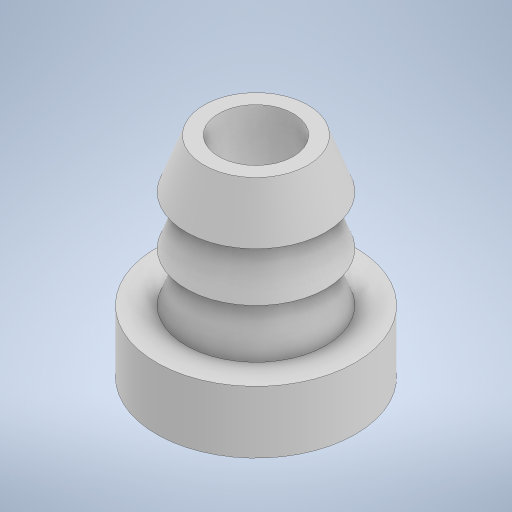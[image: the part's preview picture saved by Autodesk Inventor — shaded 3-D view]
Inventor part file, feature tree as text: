
AUTODESK INVENTOR PART (.ipt)
format: ipt  version: 2024.2 (Build 282272000, 272)  size: 631,808 bytes
history: native  units: in
note: dims shown in document units (in); Inventor stores cm internally (conversion verified against a paired STEP export)
features: sketch x3, extrude x2, revolve x1, projected_geometry x1
ambient origin geometry x8: Origin, YZ Plane, XZ Plane, XY Plane, X Axis, Y Axis, Z Axis, Center Point
bodies: Solid1 (feature_tree)
feature tree (7):
  revolve  "Revolution1"  Angle=90.0deg
  extrude  "Extrusion1"  Depth=0.075in
  extrude  "Extrusion3"  Depth=0.125in
  sketch  "Sketch1"  dims[d0=0.1406in d3=90.0deg]
  sketch  "Sketch2"  dims[d4=0.075in d5=0.4in]
  sketch  "Sketch4"  dims[d6=0.125in d7=0.0in d9=0.481in d12=0.481in d37=0.0in d38=0.0in d50=0.06in d51=0.005in d52=1.1811in d54=360.0deg]
  projected_geometry  "Projected Loop1"
